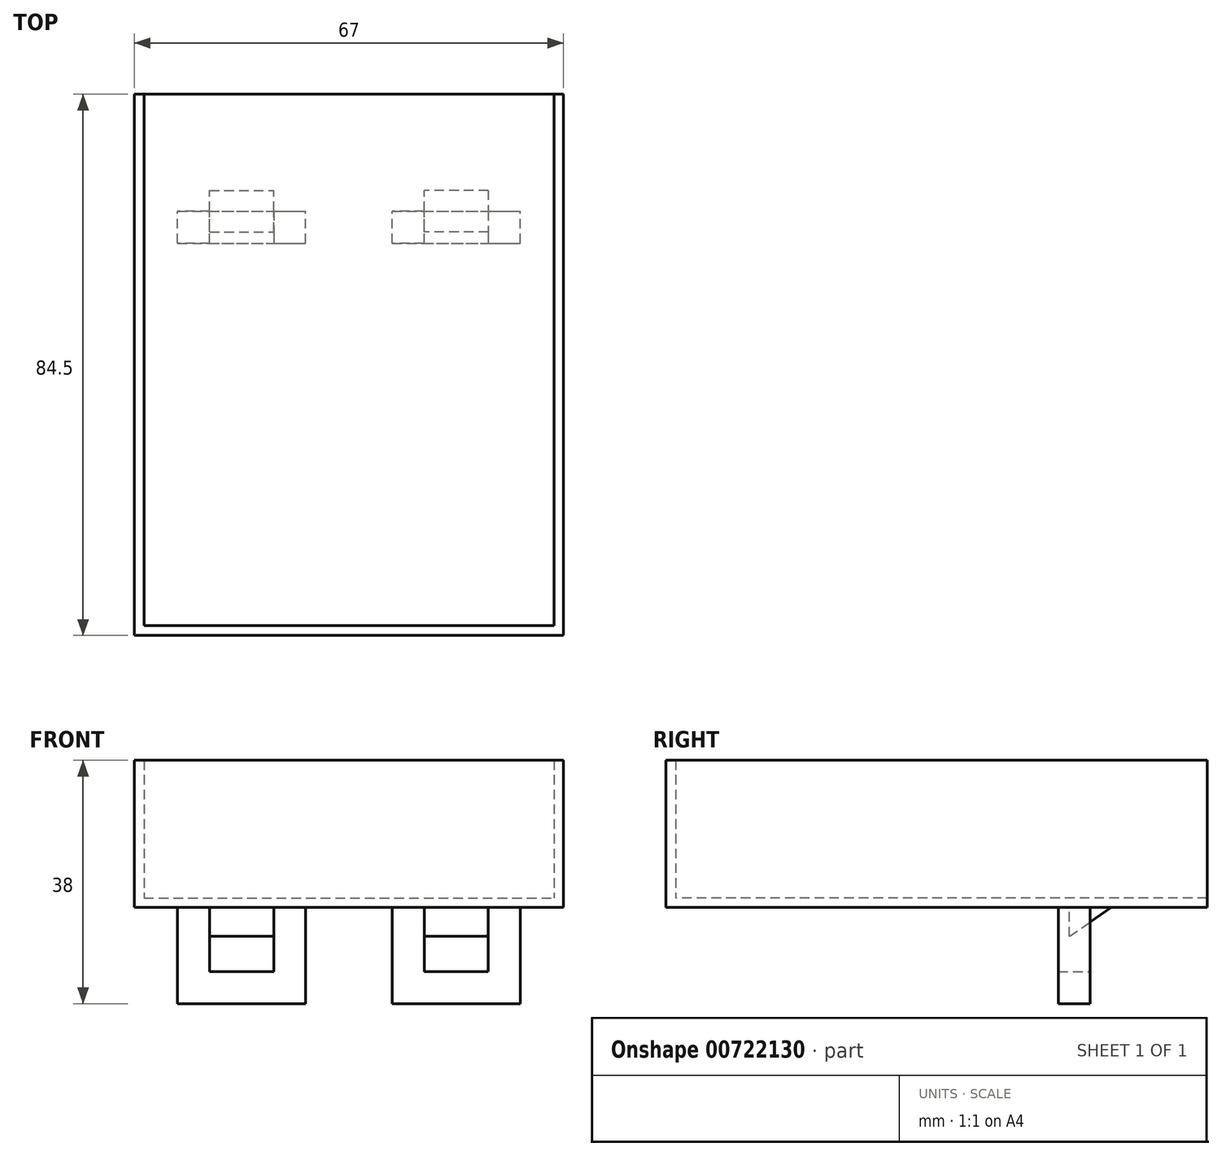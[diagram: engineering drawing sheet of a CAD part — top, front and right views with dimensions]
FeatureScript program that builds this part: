
annotation { "Feature Type Name" : "Feature", "Feature Type Description" : "" }
export const myFeature = defineFeature(function(context is Context, id is Id, definition is map)
    precondition{}
    {
        {
            var Q0;
            Q0=qCreatedBy(makeId("Top.planeOp"),FACE);
            var sketch = newSketch(context, id + "F0", { "sketchPlane" : qUnion([Q0])});
            skLineSegment(sketch, "E0.bottom", {"start": v(-33.5, 48.42) * mm, "end": v(33.5, 48.42) * mm});
            skLineSegment(sketch, "E0.top", {"start": v(-33.5, -36.08) * mm, "end": v(33.5, -36.08) * mm});
            skLineSegment(sketch, "E0.left", {"start": v(-33.5, 48.42) * mm, "end": v(-33.5, -36.08) * mm});
            skLineSegment(sketch, "E0.right", {"start": v(33.5, 48.42) * mm, "end": v(33.5, -36.08) * mm});
            skLineSegment(sketch, "E1", {"start": v(-32, 48.42) * mm, "end": v(-32, -36.08) * mm});
            skLineSegment(sketch, "E2", {"start": v(32, 48.42) * mm, "end": v(32, -36.08) * mm});
            skLineSegment(sketch, "E3", {"start": v(-32, -34.58) * mm, "end": v(32, -34.58) * mm});
            skSolve(sketch);
        }
        {
            var Q0;
            {var subQ0=sQuery(id+"F0.wireOp",EDGE,"E0.left");Q0=makeQuery(id+"F0.imprint","IMPRINT",FACE,{"disambiguationData":[TD([[makeQuery(id+"F0.imprint","IMPRINT",EDGE,{"derivedFrom":subQ0}),1.0]])]});}
            var Q1;
            {var subQ5=sQuery(id+"F0.wireOp",EDGE,"E3");Q1=makeQuery(id+"F0.imprint","IMPRINT",FACE,{"disambiguationData":[TD([[makeQuery(id+"F0.imprint","IMPRINT",EDGE,{"derivedFrom":subQ5}),-1.0]])]});}
            var Q2;
            {var subQ4=sQuery(id+"F0.wireOp",EDGE,"E0.right");Q2=makeQuery(id+"F0.imprint","IMPRINT",FACE,{"disambiguationData":[TD([[makeQuery(id+"F0.imprint","IMPRINT",EDGE,{"derivedFrom":subQ4}),-1.0]])]});}
            extrude(context, id + "F1", {"entities" : qUnion([Q0, Q1, Q2]), "depth" : 23 * mm, "offsetDistance" : 25 * mm});
        }
        {
            var Q0;
            Q0=qSketchRegion(id+"F0",true);
            extrude(context, id + "F2", {"entities" : qUnion([Q0]), "operationType" : NewBodyOperationType.ADD, "depth" : 1.5 * mm, "offsetDistance" : 25 * mm});
        }
        {
            var Q0;
            Q0=makeQuery(id+"F1.opExtrude","SWEPT_BODY",BODY,{"disambiguationData":[OSD([sQuery(id+"F0.wireOp",EDGE,"E0.bottom"),sQuery(id+"F0.wireOp",EDGE,"E0.top"),sQuery(id+"F0.wireOp",EDGE,"E0.left"),sQuery(id+"F0.wireOp",EDGE,"E0.right"),sQuery(id+"F0.wireOp",EDGE,"E1"),sQuery(id+"F0.wireOp",EDGE,"E2"),sQuery(id+"F0.wireOp",EDGE,"E3")])]});
            transform(context, id + "F3", {"entities" : qUnion([Q0]), "transformType" : TransformType.TRANSLATION_3D, "dx" : 0 * mm, "dy" : 0 * mm, "dz" : 0 * mm, "makeCopy" : true});
        }
        {
            var Q0;
            Q0=makeQuery(id+"F1.opExtrude","SWEPT_BODY",BODY,{"disambiguationData":[OSD([sQuery(id+"F0.wireOp",EDGE,"E0.bottom"),sQuery(id+"F0.wireOp",EDGE,"E0.top"),sQuery(id+"F0.wireOp",EDGE,"E0.left"),sQuery(id+"F0.wireOp",EDGE,"E0.right"),sQuery(id+"F0.wireOp",EDGE,"E1"),sQuery(id+"F0.wireOp",EDGE,"E2"),sQuery(id+"F0.wireOp",EDGE,"E3")])]});
            deleteBodies(context, id + "F4", {"entities" : qUnion([Q0])});
        }
        {
            var Q0;
            {var subQ0=sQuery(id+"F0.wireOp",EDGE,"E0.right");var subQ1=sQuery(id+"F0.wireOp",EDGE,"E0.left");var subQ2=sQuery(id+"F0.wireOp",EDGE,"E0.top");var subQ3=sQuery(id+"F0.wireOp",EDGE,"E0.bottom");Q0=makeQuery(id+"F3.opPattern","COPY",FACE,{"derivedFrom":makeQuery(id+"F2.boolean.opBoolean","MERGE",FACE,{"derivedFrom":[makeQuery(id+"F1.opExtrude","CAP_FACE",FACE,{"disambiguationData":[OSD([subQ3,subQ2,subQ1,subQ0,sQuery(id+"F0.wireOp",EDGE,"E1"),sQuery(id+"F0.wireOp",EDGE,"E2"),sQuery(id+"F0.wireOp",EDGE,"E3")])],"isStart":true}),makeQuery(id+"F2.opExtrude","CAP_FACE",FACE,{"disambiguationData":[OSD([subQ3,subQ2,subQ1,subQ0])],"isStart":true})]}),"instanceName":"1"});}
            var sketch = newSketch(context, id + "F5", { "sketchPlane" : qUnion([Q0])});
            skLineSegment(sketch, "E4.bottom", {"start": v(21.75, -28.42) * mm, "end": v(11.75, -28.42) * mm});
            skLineSegment(sketch, "E4.top", {"start": v(21.75, -26.92) * mm, "end": v(11.75, -26.92) * mm});
            skLineSegment(sketch, "E4.left", {"start": v(21.75, -28.42) * mm, "end": v(21.75, -26.92) * mm});
            skLineSegment(sketch, "E4.right", {"start": v(11.75, -28.42) * mm, "end": v(11.75, -26.92) * mm});
            skLineSegment(sketch, "E5.MirrorCS", {"start": v(-11.75, -28.42) * mm, "end": v(-11.75, -26.92) * mm});
            skLineSegment(sketch, "E6.MirrorCS", {"start": v(-21.75, -28.42) * mm, "end": v(-11.75, -28.42) * mm});
            skLineSegment(sketch, "E7.MirrorCS", {"start": v(-21.75, -28.42) * mm, "end": v(-21.75, -26.92) * mm});
            skLineSegment(sketch, "E8.MirrorCS", {"start": v(-21.75, -26.92) * mm, "end": v(-11.75, -26.92) * mm});
            skSolve(sketch);
        }
        {
            var Q0;
            Q0=makeQuery(id+"F5.imprint","IMPRINT",FACE,{"disambiguationData":[TD([[makeQuery(id+"F5.imprint","IMPRINT",EDGE,{"derivedFrom":sQuery(id+"F5.wireOp",EDGE,"E4.bottom")}),-1.0]])]});
            var Q1;
            Q1=makeQuery(id+"F5.imprint","IMPRINT",FACE,{"disambiguationData":[TD([[makeQuery(id+"F5.imprint","IMPRINT",EDGE,{"derivedFrom":sQuery(id+"F5.wireOp",EDGE,"E5.MirrorCS")}),1.0]])]});
            extrude(context, id + "F6", {"entities" : qUnion([Q0, Q1]), "operationType" : NewBodyOperationType.ADD, "depth" : 4.5 * mm, "offsetDistance" : 25 * mm});
        }
        {
            var Q0;
            Q0=makeQuery(id+"F6.opExtrude","SWEPT_FACE",FACE,{"disambiguationData":[OSD([sQuery(id+"F5.wireOp",EDGE,"E4.bottom")])]});
            var sketch = newSketch(context, id + "F7", { "sketchPlane" : qUnion([Q0])});
            skLineSegment(sketch, "E9.bottom", {"start": v(-21.75, 0) * mm, "end": v(-11.75, 0) * mm});
            skLineSegment(sketch, "E9.top", {"start": v(-21.75, -4.5) * mm, "end": v(-11.75, -4.5) * mm});
            skLineSegment(sketch, "E9.left", {"start": v(-21.75, 0) * mm, "end": v(-21.75, -4.5) * mm});
            skLineSegment(sketch, "E9.right", {"start": v(-11.75, 0) * mm, "end": v(-11.75, -4.5) * mm});
            skLineSegment(sketch, "E10.MirrorCS", {"start": v(11.75, 0) * mm, "end": v(11.75, -4.5) * mm});
            skLineSegment(sketch, "E11.MirrorCS", {"start": v(21.75, -4.5) * mm, "end": v(11.75, -4.5) * mm});
            skLineSegment(sketch, "E12.MirrorCS", {"start": v(21.75, 0) * mm, "end": v(11.75, 0) * mm});
            skLineSegment(sketch, "E13.MirrorCS", {"start": v(21.75, 0) * mm, "end": v(21.75, -4.5) * mm});
            skSolve(sketch);
        }
        {
            var Q0;
            {var subQ0=sQuery(id+"F0.wireOp",EDGE,"E0.right");var subQ1=sQuery(id+"F0.wireOp",EDGE,"E0.left");var subQ2=sQuery(id+"F0.wireOp",EDGE,"E0.top");var subQ3=sQuery(id+"F0.wireOp",EDGE,"E0.bottom");Q0=makeQuery(id+"F3.opPattern","COPY",FACE,{"derivedFrom":makeQuery(id+"F2.boolean.opBoolean","MERGE",FACE,{"derivedFrom":[makeQuery(id+"F1.opExtrude","CAP_FACE",FACE,{"disambiguationData":[OSD([subQ3,subQ2,subQ1,subQ0,sQuery(id+"F0.wireOp",EDGE,"E1"),sQuery(id+"F0.wireOp",EDGE,"E2"),sQuery(id+"F0.wireOp",EDGE,"E3")])],"isStart":true}),makeQuery(id+"F2.opExtrude","CAP_FACE",FACE,{"disambiguationData":[OSD([subQ3,subQ2,subQ1,subQ0])],"isStart":true})]}),"instanceName":"1"});}
            var sketch = newSketch(context, id + "F8", { "sketchPlane" : qUnion([Q0])});
            skLineSegment(sketch, "E14.bottom", {"start": v(-21.75, -25.17) * mm, "end": v(-26.75, -25.17) * mm});
            skLineSegment(sketch, "E14.top", {"start": v(-21.75, -30.17) * mm, "end": v(-26.75, -30.17) * mm});
            skLineSegment(sketch, "E14.left", {"start": v(-21.75, -25.17) * mm, "end": v(-21.75, -30.17) * mm});
            skLineSegment(sketch, "E14.right", {"start": v(-26.75, -25.17) * mm, "end": v(-26.75, -30.17) * mm});
            skLineSegment(sketch, "E15.bottom", {"start": v(-11.75, -25.17) * mm, "end": v(-6.75, -25.17) * mm});
            skLineSegment(sketch, "E15.top", {"start": v(-11.75, -30.17) * mm, "end": v(-6.75, -30.17) * mm});
            skLineSegment(sketch, "E15.left", {"start": v(-11.75, -25.17) * mm, "end": v(-11.75, -30.17) * mm});
            skLineSegment(sketch, "E15.right", {"start": v(-6.75, -25.17) * mm, "end": v(-6.75, -30.17) * mm});
            skLineSegment(sketch, "E16.MirrorCS", {"start": v(6.75, -25.17) * mm, "end": v(6.75, -30.17) * mm});
            skLineSegment(sketch, "E17.MirrorCS", {"start": v(11.75, -25.17) * mm, "end": v(6.75, -25.17) * mm});
            skLineSegment(sketch, "E18.MirrorCS", {"start": v(11.75, -30.17) * mm, "end": v(6.75, -30.17) * mm});
            skLineSegment(sketch, "E19.MirrorCS", {"start": v(21.75, -25.17) * mm, "end": v(21.75, -30.17) * mm});
            skLineSegment(sketch, "E20.MirrorCS", {"start": v(21.75, -25.17) * mm, "end": v(26.75, -25.17) * mm});
            skLineSegment(sketch, "E21.MirrorCS", {"start": v(26.75, -25.17) * mm, "end": v(26.75, -30.17) * mm});
            skLineSegment(sketch, "E22.MirrorCS", {"start": v(21.75, -30.17) * mm, "end": v(26.75, -30.17) * mm});
            skLineSegment(sketch, "E23.MirrorCS", {"start": v(11.75, -25.17) * mm, "end": v(11.75, -30.17) * mm});
            skPoint(sketch, "E24", {"position": v(-11.75, -27.67) * mm});
            skPoint(sketch, "E25", {"position": v(-21.75, -27.67) * mm});
            skSolve(sketch);
        }
        {
            var Q0;
            Q0=makeQuery(id+"F7.imprint","IMPRINT",FACE,{"disambiguationData":[TD([[makeQuery(id+"F7.imprint","IMPRINT",EDGE,{"derivedFrom":sQuery(id+"F7.wireOp",EDGE,"E9.bottom")}),-1.0]])]});
            var Q1;
            Q1=makeQuery(id+"F7.imprint","IMPRINT",FACE,{"disambiguationData":[TD([[makeQuery(id+"F7.imprint","IMPRINT",EDGE,{"derivedFrom":sQuery(id+"F7.wireOp",EDGE,"E10.MirrorCS")}),1.0]])]});
            extrude(context, id + "F9", {"entities" : qUnion([Q0, Q1]), "operationType" : NewBodyOperationType.ADD, "depth" : 5 * mm, "offsetDistance" : 25 * mm});
        }
        {
            var Q0;
            Q0=makeQuery(id+"F9.boolean.opBoolean","MERGE",FACE,{"derivedFrom":[makeQuery(id+"F6.opExtrude","SWEPT_FACE",FACE,{"disambiguationData":[OSD([sQuery(id+"F5.wireOp",EDGE,"E4.left")])]}),makeQuery(id+"F9.opExtrude","SWEPT_FACE",FACE,{"disambiguationData":[OSD([sQuery(id+"F7.wireOp",EDGE,"E9.left")])]})]});
            var sketch = newSketch(context, id + "F10", { "sketchPlane" : qUnion([Q0])});
            skLineSegment(sketch, "E26", {"start": v(33.42, 0) * mm, "end": v(26.92, -4.5) * mm});
            skSolve(sketch);
        }
        {
            var Q0;
            Q0 = qSketchRegion(id + "F10", true);
            var Q1;
            Q1=makeQuery(id+"F10.imprint","IMPRINT",FACE,{"disambiguationData":[TD([[makeQuery(id+"F10.imprint","IMPRINT",EDGE,{"derivedFrom":sQuery(id+"F10.wireOp",EDGE,"E26")}),1.0]])]});
            extrude(context, id + "F11", {"entities" : qUnion([Q0, Q1]), "operationType" : NewBodyOperationType.REMOVE, "oppositeDirection" : true, "depth" : 50 * mm, "offsetDistance" : 25 * mm});
        }
        {
            var Q0;
            Q0=makeQuery(id+"F8.imprint","IMPRINT",FACE,{"disambiguationData":[TD([[makeQuery(id+"F8.imprint","IMPRINT",EDGE,{"derivedFrom":sQuery(id+"F8.wireOp",EDGE,"E14.bottom")}),1.0]])]});
            var Q1;
            Q1=makeQuery(id+"F8.imprint","IMPRINT",FACE,{"disambiguationData":[TD([[makeQuery(id+"F8.imprint","IMPRINT",EDGE,{"derivedFrom":sQuery(id+"F8.wireOp",EDGE,"E15.bottom")}),-1.0]])]});
            var Q2;
            Q2=makeQuery(id+"F8.imprint","IMPRINT",FACE,{"disambiguationData":[TD([[makeQuery(id+"F8.imprint","IMPRINT",EDGE,{"derivedFrom":sQuery(id+"F8.wireOp",EDGE,"E16.MirrorCS")}),1.0]])]});
            var Q3;
            {var subQ0=sQuery(id+"F8.wireOp",EDGE,"E20.MirrorCS");Q3=makeQuery(id+"F8.imprint","IMPRINT",FACE,{"disambiguationData":[TD([[makeQuery(id+"F8.imprint","IMPRINT",EDGE,{"derivedFrom":subQ0}),-1.0]])]});}
            extrude(context, id + "F12", {"entities" : qUnion([Q0, Q1, Q2, Q3]), "operationType" : NewBodyOperationType.ADD, "depth" : 10 * mm, "offsetDistance" : 25 * mm});
        }
        {
            var Q0;
            Q0=makeQuery(id+"F12.opExtrude","SWEPT_FACE",FACE,{"disambiguationData":[OSD([sQuery(id+"F8.wireOp",EDGE,"E21.MirrorCS")])]});
            var sketch = newSketch(context, id + "F13", { "sketchPlane" : qUnion([Q0])});
            skLineSegment(sketch, "E27.bottom", {"start": v(25.17, -10) * mm, "end": v(30.17, -10) * mm});
            skLineSegment(sketch, "E27.top", {"start": v(25.17, -15) * mm, "end": v(30.17, -15) * mm});
            skLineSegment(sketch, "E27.left", {"start": v(25.17, -10) * mm, "end": v(25.17, -15) * mm});
            skLineSegment(sketch, "E27.right", {"start": v(30.17, -10) * mm, "end": v(30.17, -15) * mm});
            skSolve(sketch);
        }
        {
            var Q0;
            Q0 = qSketchRegion(id + "F13", true);
            extrude(context, id + "F14", {"entities" : qUnion([Q0]), "operationType" : NewBodyOperationType.ADD, "oppositeDirection" : true, "depth" : 53.5 * mm, "offsetDistance" : 25 * mm});
        }
        {
            var Q0;
            Q0=makeQuery(id+"F14.boolean.opBoolean","MERGE",FACE,{"derivedFrom":[makeQuery(id+"F12.opExtrude","SWEPT_FACE",FACE,{"disambiguationData":[OSD([sQuery(id+"F8.wireOp",EDGE,"E14.top")])]}),makeQuery(id+"F12.opExtrude","SWEPT_FACE",FACE,{"disambiguationData":[OSD([sQuery(id+"F8.wireOp",EDGE,"E15.top")])]}),makeQuery(id+"F12.opExtrude","SWEPT_FACE",FACE,{"disambiguationData":[OSD([sQuery(id+"F8.wireOp",EDGE,"E18.MirrorCS")])]}),makeQuery(id+"F12.opExtrude","SWEPT_FACE",FACE,{"disambiguationData":[OSD([sQuery(id+"F8.wireOp",EDGE,"E22.MirrorCS")])]}),makeQuery(id+"F14.opExtrude","SWEPT_FACE",FACE,{"disambiguationData":[OSD([sQuery(id+"F13.wireOp",EDGE,"E27.right")])]})]});
            var sketch = newSketch(context, id + "F15", { "sketchPlane" : qUnion([Q0])});
            skLineSegment(sketch, "E28.bottom", {"start": v(-6.75, -10) * mm, "end": v(6.75, -10) * mm});
            skLineSegment(sketch, "E28.top", {"start": v(-6.75, -15) * mm, "end": v(6.75, -15) * mm});
            skLineSegment(sketch, "E28.left", {"start": v(-6.75, -10) * mm, "end": v(-6.75, -15) * mm});
            skLineSegment(sketch, "E28.right", {"start": v(6.75, -10) * mm, "end": v(6.75, -15) * mm});
            skSolve(sketch);
        }
        {
            var Q0;
            Q0=makeQuery(id+"F15.imprint","IMPRINT",FACE,{"disambiguationData":[TD([[makeQuery(id+"F15.imprint","IMPRINT",EDGE,{"derivedFrom":sQuery(id+"F15.wireOp",EDGE,"E28.bottom")}),1.0]])]});
            extrude(context, id + "F16", {"entities" : qUnion([Q0]), "operationType" : NewBodyOperationType.REMOVE, "oppositeDirection" : true, "depth" : 25 * mm, "offsetDistance" : 25 * mm});
        }
    });
